# Revit family: 3f_filippi_-_3f_66_3f_filippi_-_8357_-_3f_66_1_led_6_ii
name_source: partatom
category: Lighting Fixtures
units: mm (PartAtom-declared; Revit-internal decimal feet)

## family parameters
Cut with Voids When Loaded = No
Host = Face
Light Source = No
Part Type = Normal
Room Calculation Point = No
Round Connector Dimension = Use Diameter
Shared = No

## types (1)
- 3F Filippi - 3F 66 (1 x LED, 774 lm, 9 W, 4000 K)
    Apparent Load = 9 VA
    Approval mark = ENEC
    CIE Flux Codes = 25 59 96 99 100
    Color Rendering = 80
    Color Temperature = 4000 K
    Control Gear = Electronic ballast
    Default Elevation = 1800 mm
    Description = ILLUMINOTECHNICAL
Luminous efficiency 100% (DLOR 99%, ULOR 1%).
Initial luminous flux of the luminaire 774 lm.
Downward bilateral distribution.
BUG (Backlight, Uplight, Glare) IESNA TM-15: B1 U1 G1.
Beam angle: 55° - 119°.
Luminous efficacy 86 lm/W.
Lifetime (L75/B10): 30000 h. (tq+25°C)
Lifetime (L70/B10): 50000 h. (tq+25°C)
Sudden decreased luminous flux after 50000 hours: 0% (C0).
Photobiological safety in compliance with IEC/TR 62778: RG0 risk exempt, (IEC 62471).
In compliance with IEC/EN 62722-2-1 - IEC/EN 62717 standards.

SOURCE
LED module 6W/840.
Energy efficiency class (UE 2019/2020 - UE 2019/2015): E.
CIE 13.3 Colour rendering index: CRI >80 (R9 <50%).
IES TM-30 Fidelity Index: Rf = 84 Rg = 95.
CCT nominal colour temperature 4000 K.
Colour initial tolerance (MacAdam): SDCM 4.

MECHANICAL
Self-extinguishing V2 polycarbonate housing, injection moulded, RAL 7035 grey.
Flow recuperator in specular aluminium with superficial titanium-magnesium treatment, non-iridescent.
Transparent methacrylate (PMMA) diffuser, injection moulded, with smooth outer surface and differentiated prismatic inner surface.
Sealing gaskets between housing and diffuser in ecological anti-aging EPDM.
Diffuser safety seal with 4 latches attaching it to the housing, in stainless steel.
Luminaire with limited surface temperature. - D - (EN 60598-2-24)
Dimensions: 255x176 mm, height 344 mm. Weight 2.1 kg.
IP65 protection degree.
Mechanical strength to impacts IK08 (5 joule).
Glow-wire test resistance 650°C.

ELECTRICAL
Halogen Free electronic wiring 230V-50/60Hz, power factor 0.90, THD <25%, constant output current, SELV, class II, 1 driver.
Power of the luminaire 9 W.
CE - IEC 60598-1 - EN 60598-1.
Flicker: <5%.
Ambient temperature from 0°C to +25°C.
Temperature class T6 max 85°C.
Line entry at rear through rubber seal or at side after drilling.
Relative humidity UR: <85%.

INSTALLATION
Wall.

APPLICATIONS
Wall mounting, particularly suitable for outdoor lighting of civil and industrial buildings, porticos, underpasses and walkways.
Controlled bilateral distribution provides uniform lighting on work surfaces.
Control of light pollution as per UNI EN 12464-2.

WARNING
Luminaire designed for disposal/recycling at end-of-life.
Replaceable (LED only) light source by a professional. Replaceable control gear by a professional.
    Height = 344 mm
    Lamp = 1 x LED
    Lamp Light Flux = 774 lm
    Lamp Power = 9 W
    Lamp count = 1
    Length = 255 mm
    Lifetime = 50000 h
    Luminous efficacy = 86 lm/W
    Manufacturer = 3F Filippi
    ModVariant = No
    Model = 3F Filippi - 8357 - 3F 66 1 LED 6 II
    Mounting Place = Wall
    Mounting Type = Surface mounted
    Number of Poles = 1
    OnlyDefault = Yes
    Power Factor = 1
    Product Name = 3F Filippi - 3F 66
    Product group = wall-mounted luminaire
    ProductGroupID = 20
    Protection Class = Protection class II
    Protection Degree = IP 65
    RLX_Detail_Level = 1
    RLX_Emergency_Light_Flux = 0 lm
    RLX_Emergency_Type = 0
    RLX_Emergency_Type_DB = No
    RlxData = <blob elided: 78101 chars, md5=22c39392>
    Socket = socket
    Standby Power = 0 W
    System Light Flux = 774 lm
    System Power = 9 W
    Type Comments = Product without accessories
    Type Image = 3ffilippi_8357.jpg
    URL = http://relux.com
    VarID = ---
    Voltage = 0 V
    Weight = 0.00 kg
    Width = 176 mm

## geometry (parser evidence)
native form markers: Sweep x12
no freeform markers — native parametric forms only
